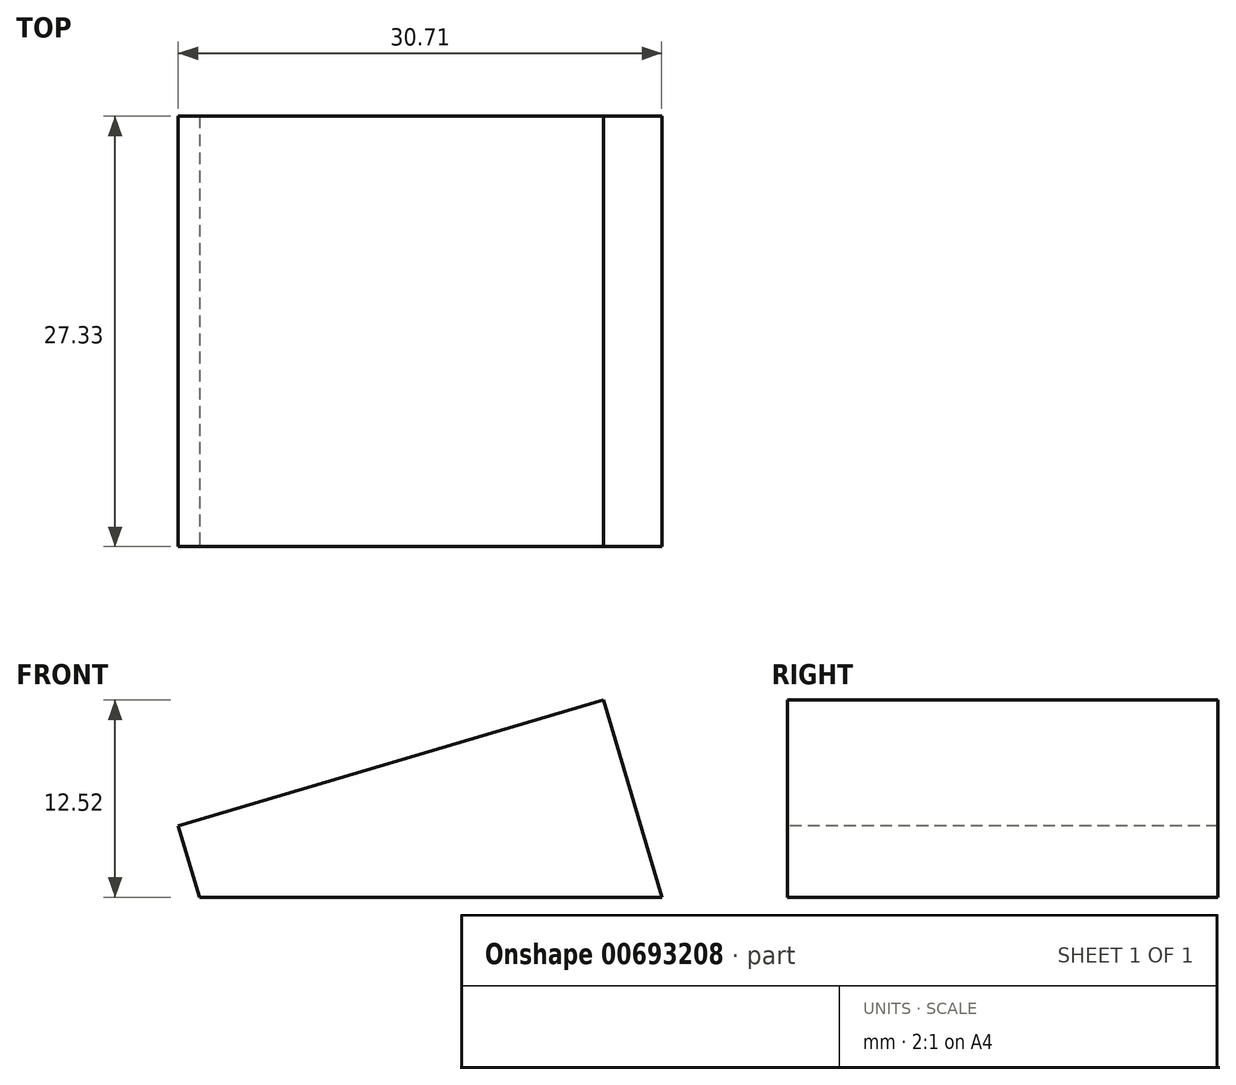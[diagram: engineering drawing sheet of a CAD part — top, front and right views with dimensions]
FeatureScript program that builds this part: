
annotation { "Feature Type Name" : "Feature", "Feature Type Description" : "" }
export const myFeature = defineFeature(function(context is Context, id is Id, definition is map)
    precondition{}
    {
        {
            var Q0;
            Q0=qCreatedBy(makeId("Front.planeOp"),FACE);
            cPlane(context, id + "F0", {"entities" : qUnion([Q0]), "cplaneType" : CPlaneType.OFFSET, "offset" : 13.5 * mm, "width" : 150 * mm, "height" : 150 * mm});
        }
        {
            var Q0;
            Q0=qCreatedBy(id+"F0.planeOp",FACE);
            var sketch = newSketch(context, id + "F1", { "sketchPlane" : qUnion([Q0])});
            skPoint(sketch, "E0", {"position": v(-36.48, 44.57) * mm});
            skLineSegment(sketch, "E1", {"start": v(-14.88, 10) * mm, "end": v(12.12, 10) * mm});
            skLineSegment(sketch, "E2", {"start": v(12.12, 10) * mm, "end": v(12.12, 18) * mm});
            skLineSegment(sketch, "E3", {"start": v(12.12, 18) * mm, "end": v(-14.88, 10) * mm});
            skLineSegment(sketch, "E4", {"start": v(12.12, 18) * mm, "end": v(15.83, 5.48) * mm});
            skLineSegment(sketch, "E5", {"start": v(-14.88, 10) * mm, "end": v(-13.54, 5.48) * mm});
            skLineSegment(sketch, "E6", {"start": v(-13.54, 5.48) * mm, "end": v(15.83, 5.48) * mm});
            skSolve(sketch);
        }
        {
            var Q0;
            Q0 = qSketchRegion(id + "F1", true);
            extrude(context, id + "F2", {"entities" : qUnion([Q0]), "oppositeDirection" : true, "depth" : 27.33 * mm, "offsetDistance" : 25 * mm});
        }
        {
            var Q0;
            Q0=makeQuery(id+"F2.opExtrude","SWEPT_FACE",FACE,{"disambiguationData":[OSD([sQuery(id+"F1.wireOp",EDGE,"E3")])]});
            var sketch = newSketch(context, id + "F3", { "sketchPlane" : qUnion([Q0])});
            skCircle(sketch, "E7", {"center": v(2.99, 0) * mm, "radius": 11.5 * mm});
            skArc(sketch, "E8.0", {"start": v(-0.01, 13.16) * mm, "mid": v(2.99, -13.5) * mm, "end": v(5.99, 13.16) * mm});
            skLineSegment(sketch, "E9.bottom", {"start": v(5.99, 13.16) * mm, "end": v(-0.01, 13.16) * mm});
            skLineSegment(sketch, "E9.top", {"start": v(5.99, 13.84) * mm, "end": v(-0.01, 13.84) * mm});
            skLineSegment(sketch, "E9.left", {"start": v(5.99, 13.16) * mm, "end": v(5.99, 13.84) * mm});
            skLineSegment(sketch, "E9.right", {"start": v(-0.01, 13.16) * mm, "end": v(-0.01, 13.84) * mm});
            skLineSegment(sketch, "E10.0", {"start": v(-8.5, 7.13) * mm, "end": v(-6.84, 5.97) * mm, "construction": true});
            skLineSegment(sketch, "E11.0", {"start": v(-7.64, 8.36) * mm, "end": v(-5.98, 7.2) * mm, "construction": true});
            skLineSegment(sketch, "E12.0", {"start": v(-10.4, -0.75) * mm, "end": v(-8.49, -0.75) * mm, "construction": true});
            skLineSegment(sketch, "E13.0", {"start": v(-10.4, 0.75) * mm, "end": v(-8.49, 0.75) * mm, "construction": true});
            skLineSegment(sketch, "E14.0", {"start": v(13.58, 8.37) * mm, "end": v(11.94, 7.22) * mm, "construction": true});
            skLineSegment(sketch, "E15.0", {"start": v(14.44, 7.14) * mm, "end": v(12.8, 6) * mm, "construction": true});
            skLineSegment(sketch, "E16.trimOffspring", {"start": v(1.99, -11.46) * mm, "end": v(1.99, -13.5) * mm, "construction": true});
            skLineSegment(sketch, "E17.trimOffspring", {"start": v(3.99, -11.46) * mm, "end": v(3.99, -13.5) * mm, "construction": true});
            skLineSegment(sketch, "E18.trimOffspring", {"start": v(14.46, 0.75) * mm, "end": v(16.6, 0.75) * mm, "construction": true});
            skLineSegment(sketch, "E19.trimOffspring", {"start": v(14.46, -0.75) * mm, "end": v(16.6, -0.75) * mm, "construction": true});
            skLineSegment(sketch, "E20.trimOffspring", {"start": v(11.96, -7.2) * mm, "end": v(13.62, -8.36) * mm, "construction": true});
            skLineSegment(sketch, "E21.trimOffspring", {"start": v(-6, -7.17) * mm, "end": v(-7.68, -8.34) * mm, "construction": true});
            skLineSegment(sketch, "E22.trimOffspring", {"start": v(-6.86, -5.94) * mm, "end": v(-8.54, -7.12) * mm, "construction": true});
            skLineSegment(sketch, "E23.trimOffspring", {"start": v(12.82, -5.97) * mm, "end": v(14.48, -7.13) * mm, "construction": true});
            skSolve(sketch);
        }
    });
